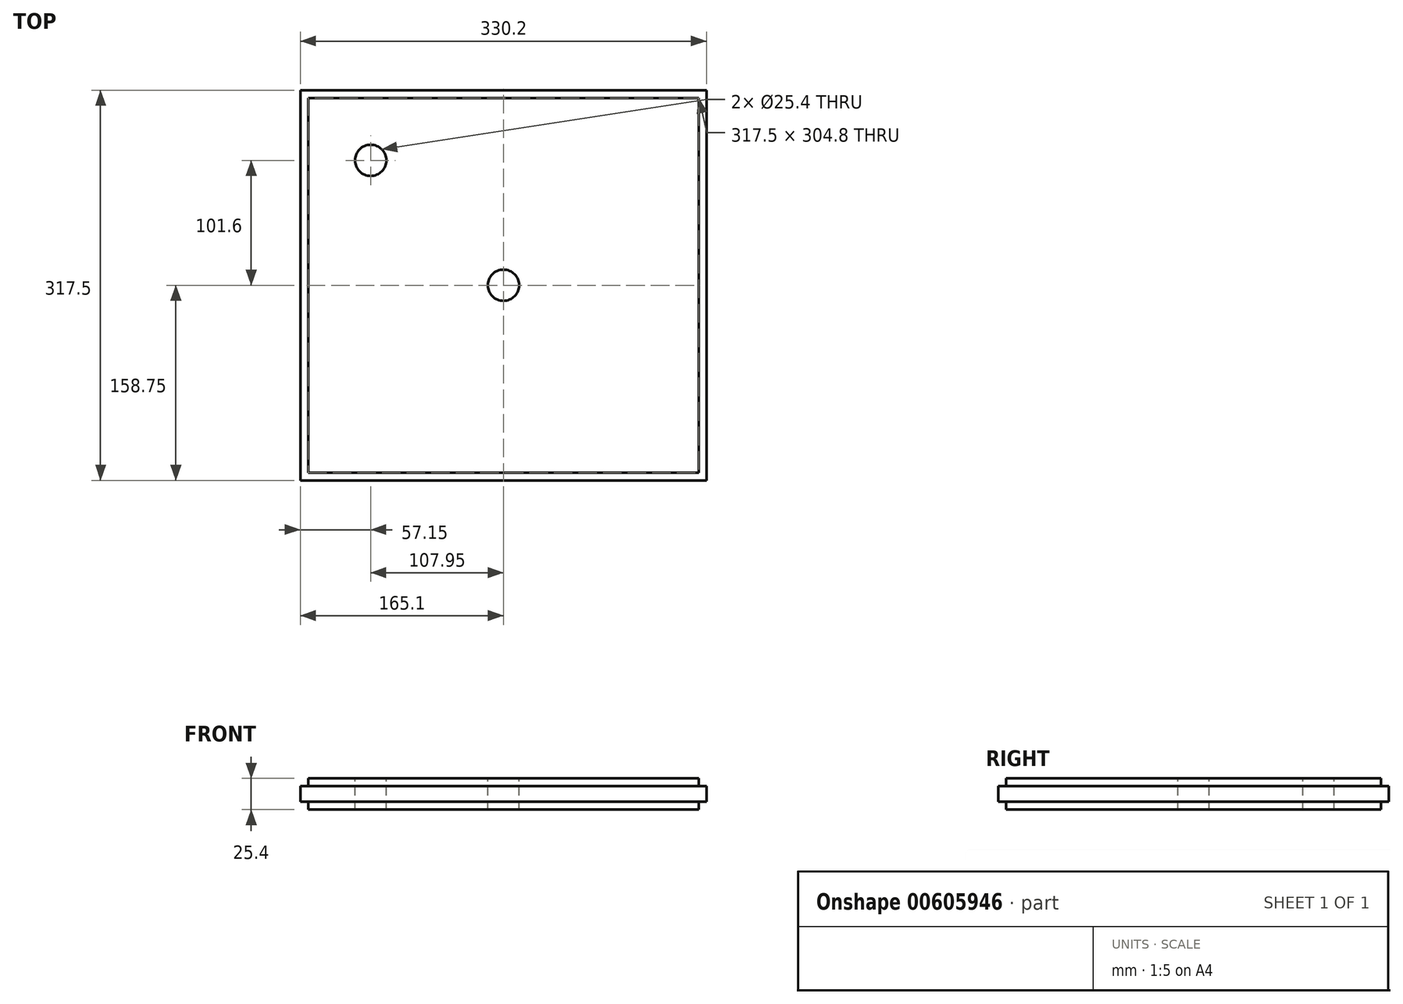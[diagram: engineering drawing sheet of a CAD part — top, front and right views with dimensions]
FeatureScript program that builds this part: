
annotation { "Feature Type Name" : "Feature", "Feature Type Description" : "" }
export const myFeature = defineFeature(function(context is Context, id is Id, definition is map)
    precondition{}
    {
        {
            var Q0;
            Q0=qCreatedBy(makeId("Top.planeOp"),FACE);
            var sketch = newSketch(context, id + "F0", { "sketchPlane" : qUnion([Q0])});
            skLineSegment(sketch, "E0.bottom", {"start": v(158.75, 152.4) * mm, "end": v(-158.75, 152.4) * mm});
            skLineSegment(sketch, "E0.top", {"start": v(158.75, -152.4) * mm, "end": v(-158.75, -152.4) * mm});
            skLineSegment(sketch, "E0.left", {"start": v(158.75, 152.4) * mm, "end": v(158.75, -152.4) * mm});
            skLineSegment(sketch, "E0.right", {"start": v(-158.75, 152.4) * mm, "end": v(-158.75, -152.4) * mm});
            skPoint(sketch, "E0.middle", {"position": v(0, 0) * mm});
            skSolve(sketch);
        }
        {
            var Q0;
            Q0=makeQuery(id+"F0.imprint","IMPRINT",FACE,{"disambiguationData":[TD([[makeQuery(id+"F0.imprint","IMPRINT",EDGE,{"derivedFrom":sQuery(id+"F0.wireOp",EDGE,"E0.bottom")}),1.0]])]});
            extrude(context, id + "F1", {"entities" : qUnion([Q0]), "depth" : 25.4 * mm, "offsetDistance" : 25.4 * mm});
        }
        {
            var Q0;
            Q0=makeQuery(id+"F1.opExtrude","SWEPT_FACE",FACE,{"disambiguationData":[OSD([sQuery(id+"F0.wireOp",EDGE,"E0.top")])]});
            var sketch = newSketch(context, id + "F2", { "sketchPlane" : qUnion([Q0])});
            skLineSegment(sketch, "E1", {"start": v(-158.75, 0) * mm, "end": v(-158.75, 6.35) * mm});
            skLineSegment(sketch, "E2", {"start": v(-158.75, 6.35) * mm, "end": v(-158.75, 19.05) * mm});
            skLineSegment(sketch, "E3", {"start": v(-158.75, 19.05) * mm, "end": v(158.75, 19.05) * mm});
            skLineSegment(sketch, "E4", {"start": v(158.75, 19.05) * mm, "end": v(158.75, 6.35) * mm});
            skLineSegment(sketch, "E5", {"start": v(158.75, 6.35) * mm, "end": v(-158.75, 6.35) * mm});
            skSolve(sketch);
        }
        {
            var Q0;
            Q0=makeQuery(id+"F2.imprint","IMPRINT",FACE,{"disambiguationData":[TD([[makeQuery(id+"F2.imprint","IMPRINT",EDGE,{"derivedFrom":sQuery(id+"F2.wireOp",EDGE,"E2")}),1.0]])]});
            extrude(context, id + "F3", {"entities" : qUnion([Q0]), "operationType" : NewBodyOperationType.ADD, "depth" : 6.35 * mm, "offsetDistance" : 25.4 * mm});
        }
        {
            var Q0;
            Q0=makeQuery(id+"F1.opExtrude","SWEPT_FACE",FACE,{"disambiguationData":[OSD([sQuery(id+"F0.wireOp",EDGE,"E0.bottom")])]});
            var sketch = newSketch(context, id + "F4", { "sketchPlane" : qUnion([Q0])});
            skLineSegment(sketch, "E6", {"start": v(-158.75, 0) * mm, "end": v(-158.75, 6.35) * mm});
            skLineSegment(sketch, "E7", {"start": v(-158.75, 6.35) * mm, "end": v(-158.75, 19.05) * mm});
            skLineSegment(sketch, "E8", {"start": v(158.75, 19.05) * mm, "end": v(-158.75, 19.05) * mm});
            skLineSegment(sketch, "E9", {"start": v(158.75, 19.05) * mm, "end": v(158.75, 6.35) * mm});
            skLineSegment(sketch, "E10", {"start": v(158.75, 6.35) * mm, "end": v(-158.75, 6.35) * mm});
            skSolve(sketch);
        }
        {
            var Q0;
            Q0=makeQuery(id+"F4.imprint","IMPRINT",FACE,{"disambiguationData":[TD([[makeQuery(id+"F4.imprint","IMPRINT",EDGE,{"derivedFrom":sQuery(id+"F4.wireOp",EDGE,"E7")}),1.0]])]});
            extrude(context, id + "F5", {"entities" : qUnion([Q0]), "operationType" : NewBodyOperationType.ADD, "depth" : 6.35 * mm, "offsetDistance" : 25.4 * mm});
        }
        {
            var Q0;
            Q0=makeQuery(id+"F5.boolean.opBoolean","MERGE",FACE,{"derivedFrom":[makeQuery(id+"F3.boolean.opBoolean","MERGE",FACE,{"derivedFrom":[makeQuery(id+"F1.opExtrude","SWEPT_FACE",FACE,{"disambiguationData":[OSD([sQuery(id+"F0.wireOp",EDGE,"E0.left")])]}),makeQuery(id+"F3.opExtrude","SWEPT_FACE",FACE,{"disambiguationData":[OSD([sQuery(id+"F2.wireOp",EDGE,"E4")])]})]}),makeQuery(id+"F5.opExtrude","SWEPT_FACE",FACE,{"disambiguationData":[OSD([sQuery(id+"F4.wireOp",EDGE,"E7")])]})]});
            var sketch = newSketch(context, id + "F6", { "sketchPlane" : qUnion([Q0])});
            skLineSegment(sketch, "E11.bottom", {"start": v(-158.75, 19.05) * mm, "end": v(158.75, 19.05) * mm});
            skLineSegment(sketch, "E11.top", {"start": v(-158.75, 6.35) * mm, "end": v(158.75, 6.35) * mm});
            skLineSegment(sketch, "E11.left", {"start": v(-158.75, 19.05) * mm, "end": v(-158.75, 6.35) * mm});
            skLineSegment(sketch, "E11.right", {"start": v(158.75, 19.05) * mm, "end": v(158.75, 6.35) * mm});
            skSolve(sketch);
        }
        {
            var Q0;
            Q0=makeQuery(id+"F5.boolean.opBoolean","MERGE",FACE,{"derivedFrom":[makeQuery(id+"F3.boolean.opBoolean","MERGE",FACE,{"derivedFrom":[makeQuery(id+"F1.opExtrude","SWEPT_FACE",FACE,{"disambiguationData":[OSD([sQuery(id+"F0.wireOp",EDGE,"E0.right")])]}),makeQuery(id+"F3.opExtrude","SWEPT_FACE",FACE,{"disambiguationData":[OSD([sQuery(id+"F2.wireOp",EDGE,"E2")])]})]}),makeQuery(id+"F5.opExtrude","SWEPT_FACE",FACE,{"disambiguationData":[OSD([sQuery(id+"F4.wireOp",EDGE,"E9")])]})]});
            var sketch = newSketch(context, id + "F7", { "sketchPlane" : qUnion([Q0])});
            skLineSegment(sketch, "E12.bottom", {"start": v(-158.75, 19.05) * mm, "end": v(158.75, 19.05) * mm});
            skLineSegment(sketch, "E12.top", {"start": v(-158.75, 6.35) * mm, "end": v(158.75, 6.35) * mm});
            skLineSegment(sketch, "E12.left", {"start": v(-158.75, 19.05) * mm, "end": v(-158.75, 6.35) * mm});
            skLineSegment(sketch, "E12.right", {"start": v(158.75, 19.05) * mm, "end": v(158.75, 6.35) * mm});
            skSolve(sketch);
        }
        {
            var Q0;
            {var subQ15=sQuery(id+"F7.wireOp",EDGE,"E12.left");Q0=makeQuery(id+"F7.imprint","IMPRINT",FACE,{"disambiguationData":[TD([[makeQuery(id+"F7.imprint","IMPRINT",EDGE,{"derivedFrom":subQ15}),1.0]])]});}
            extrude(context, id + "F8", {"entities" : qUnion([Q0]), "operationType" : NewBodyOperationType.ADD, "depth" : 6.35 * mm, "offsetDistance" : 25.4 * mm});
        }
        {
            var Q0;
            {var subQ15=sQuery(id+"F6.wireOp",EDGE,"E11.left");Q0=makeQuery(id+"F6.imprint","IMPRINT",FACE,{"disambiguationData":[TD([[makeQuery(id+"F6.imprint","IMPRINT",EDGE,{"derivedFrom":subQ15}),1.0]])]});}
            extrude(context, id + "F9", {"entities" : qUnion([Q0]), "operationType" : NewBodyOperationType.ADD, "depth" : 6.35 * mm, "offsetDistance" : 25.4 * mm});
        }
        {
            var Q0;
            Q0=makeQuery(id+"F1.opExtrude","CAP_FACE",FACE,{"disambiguationData":[OSD([sQuery(id+"F0.wireOp",EDGE,"E0.bottom"),sQuery(id+"F0.wireOp",EDGE,"E0.top"),sQuery(id+"F0.wireOp",EDGE,"E0.left"),sQuery(id+"F0.wireOp",EDGE,"E0.right")])],"isStart":false});
            var sketch = newSketch(context, id + "F10", { "sketchPlane" : qUnion([Q0])});
            skCircle(sketch, "E13", {"center": v(-107.95, 101.6) * mm, "radius": 12.7 * mm});
            skSolve(sketch);
        }
        {
            var Q0;
            Q0=makeQuery(id+"F10.imprint","IMPRINT",FACE,{"disambiguationData":[TD([[makeQuery(id+"F10.imprint","IMPRINT",EDGE,{"derivedFrom":sQuery(id+"F10.wireOp",EDGE,"E13")}),1.0]])]});
            extrude(context, id + "F11", {"entities" : qUnion([Q0]), "operationType" : NewBodyOperationType.REMOVE, "oppositeDirection" : true, "depth" : 25.4 * mm, "offsetDistance" : 25.4 * mm});
        }
        {
            var Q0;
            Q0=makeQuery(id+"F1.opExtrude","CAP_FACE",FACE,{"disambiguationData":[OSD([sQuery(id+"F0.wireOp",EDGE,"E0.bottom"),sQuery(id+"F0.wireOp",EDGE,"E0.top"),sQuery(id+"F0.wireOp",EDGE,"E0.left"),sQuery(id+"F0.wireOp",EDGE,"E0.right")])],"isStart":false});
            var sketch = newSketch(context, id + "F12", { "sketchPlane" : qUnion([Q0])});
            skCircle(sketch, "E14", {"center": v(0, 0) * mm, "radius": 12.7 * mm});
            skSolve(sketch);
        }
        {
            var Q0;
            Q0=makeQuery(id+"F12.imprint","IMPRINT",FACE,{"disambiguationData":[TD([[makeQuery(id+"F12.imprint","IMPRINT",EDGE,{"derivedFrom":sQuery(id+"F12.wireOp",EDGE,"E14")}),1.0]])]});
            extrude(context, id + "F13", {"entities" : qUnion([Q0]), "operationType" : NewBodyOperationType.REMOVE, "oppositeDirection" : true, "depth" : 25.4 * mm, "offsetDistance" : 25.4 * mm});
        }
    });
